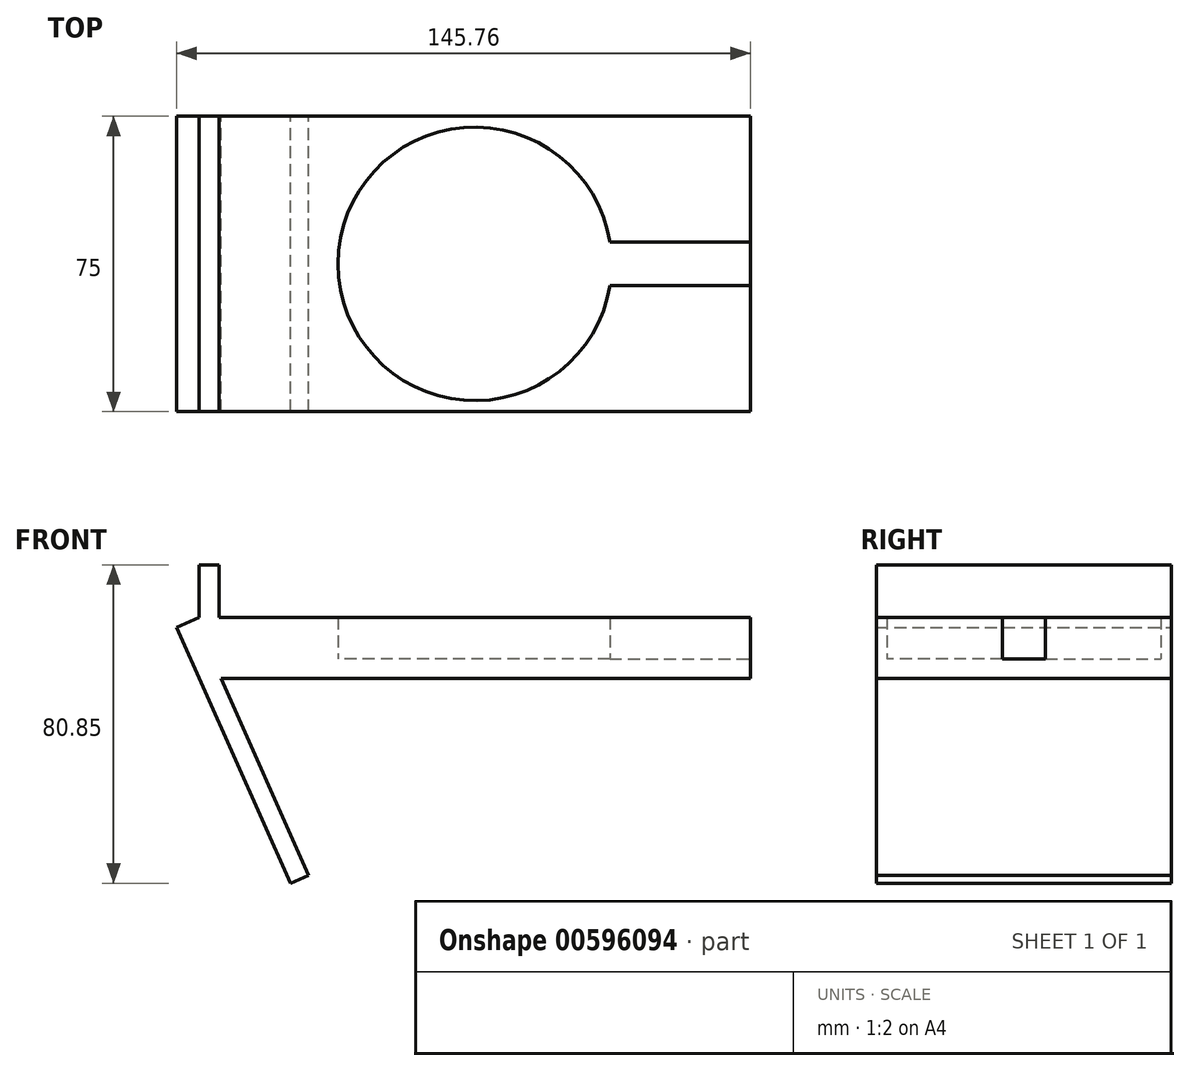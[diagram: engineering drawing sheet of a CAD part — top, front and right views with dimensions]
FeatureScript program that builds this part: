
annotation { "Feature Type Name" : "Feature", "Feature Type Description" : "" }
export const myFeature = defineFeature(function(context is Context, id is Id, definition is map)
    precondition{}
    {
        {
            var Q0;
            Q0=qCreatedBy(makeId("Top.planeOp"),FACE);
            var sketch = newSketch(context, id + "F0", { "sketchPlane" : qUnion([Q0])});
            skLineSegment(sketch, "E0.bottom", {"start": v(70, -37.5) * mm, "end": v(-70, -37.5) * mm});
            skLineSegment(sketch, "E0.top", {"start": v(70, 37.5) * mm, "end": v(-70, 37.5) * mm});
            skLineSegment(sketch, "E0.left", {"start": v(70, -37.5) * mm, "end": v(70, 37.5) * mm});
            skLineSegment(sketch, "E0.right", {"start": v(-70, -37.5) * mm, "end": v(-70, 37.5) * mm});
            skPoint(sketch, "E0.middle", {"position": v(0, 0) * mm});
            skLineSegment(sketch, "E1.bottom", {"start": v(34.31, 5.5) * mm, "end": v(70, 5.5) * mm});
            skLineSegment(sketch, "E1.top", {"start": v(34.31, -5.5) * mm, "end": v(70, -5.5) * mm});
            skLineSegment(sketch, "E1.left", {"start": v(34.31, 5.5) * mm, "end": v(34.31, -5.5) * mm, "construction": true});
            skLineSegment(sketch, "E1.right", {"start": v(70, 5.5) * mm, "end": v(70, -5.5) * mm});
            skPoint(sketch, "E2", {"position": v(34.31, 0) * mm});
            skArc(sketch, "E3", {"start": v(34.31, 5.5) * mm, "mid": v(-34.75, 0) * mm, "end": v(34.31, -5.5) * mm});
            skSolve(sketch);
        }
        {
            var Q0;
            {var subQ4=sQuery(id+"F0.wireOp",EDGE,"E0.bottom");Q0=makeQuery(id+"F0.imprint","IMPRINT",FACE,{"disambiguationData":[TD([[makeQuery(id+"F0.imprint","IMPRINT",EDGE,{"derivedFrom":subQ4}),-1.0]])]});}
            extrude(context, id + "F1", {"entities" : qUnion([Q0]), "depth" : 10.5 * mm, "offsetDistance" : 25 * mm});
        }
        {
            var Q0;
            Q0=qCreatedBy(makeId("Top.planeOp"),FACE);
            var sketch = newSketch(context, id + "F2", { "sketchPlane" : qUnion([Q0])});
            skLineSegment(sketch, "E4.bottom", {"start": v(70, 37.5) * mm, "end": v(-70, 37.5) * mm});
            skLineSegment(sketch, "E4.top", {"start": v(70, -37.5) * mm, "end": v(-70, -37.5) * mm});
            skLineSegment(sketch, "E4.left", {"start": v(70, 37.5) * mm, "end": v(70, -37.5) * mm});
            skLineSegment(sketch, "E4.right", {"start": v(-70, 37.5) * mm, "end": v(-70, -37.5) * mm});
            skPoint(sketch, "E4.middle", {"position": v(0, 0) * mm});
            skSolve(sketch);
        }
        {
            var Q0;
            Q0 = qSketchRegion(id + "F2", true);
            extrude(context, id + "F3", {"entities" : qUnion([Q0]), "operationType" : NewBodyOperationType.ADD, "oppositeDirection" : true, "depth" : 5 * mm, "offsetDistance" : 25 * mm});
        }
        {
            var Q0;
            Q0=qCreatedBy(makeId("Front.planeOp"),FACE);
            var sketch = newSketch(context, id + "F4", { "sketchPlane" : qUnion([Q0])});
            skLineSegment(sketch, "E5.0.0", {"start": v(-70, 10.5) * mm, "end": v(-70, -5) * mm});
            skLineSegment(sketch, "E5.0.1", {"start": v(-70, -5) * mm, "end": v(70, -5) * mm});
            skLineSegment(sketch, "E5.0.2", {"start": v(70, -5) * mm, "end": v(70, 10.5) * mm});
            skLineSegment(sketch, "E5.0.3", {"start": v(70, 10.5) * mm, "end": v(-70, 10.5) * mm});
            skLineSegment(sketch, "E6.bottom", {"start": v(-70, -5) * mm, "end": v(-65.43, -2.97) * mm});
            skLineSegment(sketch, "E6.top", {"start": v(-46.84, -57.02) * mm, "end": v(-42.28, -54.98) * mm});
            skLineSegment(sketch, "E6.left", {"start": v(-70, -5) * mm, "end": v(-46.84, -57.02) * mm});
            skLineSegment(sketch, "E6.right", {"start": v(-65.43, -2.97) * mm, "end": v(-42.28, -54.98) * mm});
            skLineSegment(sketch, "E7", {"start": v(-46.84, -57.02) * mm, "end": v(70, -5) * mm, "construction": true});
            skLineSegment(sketch, "E8", {"start": v(-70, 10.5) * mm, "end": v(-75.76, 7.94) * mm});
            skLineSegment(sketch, "E9", {"start": v(-75.76, 7.94) * mm, "end": v(-70, -5) * mm});
            skSolve(sketch);
        }
        {
            var Q0;
            Q0 = qSketchRegion(id + "F4", true);
            var Q1;
            Q1=makeQuery(id+"F3.boolean.opBoolean","MERGE",FACE,{"derivedFrom":[makeQuery(id+"F1.opExtrude","SWEPT_FACE",FACE,{"disambiguationData":[OSD([sQuery(id+"F0.wireOp",EDGE,"E0.bottom")])]}),makeQuery(id+"F3.opExtrude","SWEPT_FACE",FACE,{"disambiguationData":[OSD([sQuery(id+"F2.wireOp",EDGE,"E4.top")])]})]});
            var Q2;
            Q2=makeQuery(id+"F3.boolean.opBoolean","MERGE",FACE,{"derivedFrom":[makeQuery(id+"F1.opExtrude","SWEPT_FACE",FACE,{"disambiguationData":[OSD([sQuery(id+"F0.wireOp",EDGE,"E0.top")])]}),makeQuery(id+"F3.opExtrude","SWEPT_FACE",FACE,{"disambiguationData":[OSD([sQuery(id+"F2.wireOp",EDGE,"E4.bottom")])]})]});
            extrude(context, id + "F5", {"entities" : qUnion([Q0]), "operationType" : NewBodyOperationType.ADD, "endBound" : BoundingType.UP_TO_SURFACE, "depth" : 25 * mm, "endBoundEntityFace" : qUnion([Q1]), "offsetDistance" : 25 * mm, "hasSecondDirection" : true, "secondDirectionBound" : SecondDirectionBoundingType.UP_TO_SURFACE, "secondDirectionOppositeDirection" : true, "secondDirectionDepth" : 25 * mm, "secondDirectionBoundEntityFace" : qUnion([Q2])});
        }
        {
            var Q0;
            Q0=makeQuery(id+"F0.imprint","IMPRINT",FACE,{"disambiguationData":[TD([[makeQuery(id+"F0.imprint","IMPRINT",EDGE,{"derivedFrom":sQuery(id+"F0.wireOp",EDGE,"E1.bottom")}),-1.0]])]});
            var Q1;
            Q1=sQuery(id+"F0.wireOp",EDGE,"E3");
            var Q2;
            Q2=sQuery(id+"F0.wireOp",EDGE,"E1.bottom");
            var Q3;
            Q3=sQuery(id+"F0.wireOp",EDGE,"E1.right");
            var Q4;
            Q4=sQuery(id+"F0.wireOp",EDGE,"E1.top");
            var Q5;
            Q5=makeQuery(id+"F5.boolean.opBoolean","MERGE",FACE,{"derivedFrom":[makeQuery(id+"F1.opExtrude","CAP_FACE",FACE,{"disambiguationData":[OSD([sQuery(id+"F0.wireOp",EDGE,"E0.bottom"),sQuery(id+"F0.wireOp",EDGE,"E0.top"),sQuery(id+"F0.wireOp",EDGE,"E0.left"),sQuery(id+"F0.wireOp",EDGE,"E0.right"),sQuery(id+"F0.wireOp",EDGE,"E1.bottom"),sQuery(id+"F0.wireOp",EDGE,"E1.top"),sQuery(id+"F0.wireOp",EDGE,"E3")])],"isStart":false}),makeQuery(id+"F5.opExtrude","SWEPT_FACE",FACE,{"disambiguationData":[OSD([sQuery(id+"F4.wireOp",EDGE,"E5.0.3")])]})]});
            extrude(context, id + "F6", {"entities" : qUnion([Q0]), "operationType" : NewBodyOperationType.REMOVE, "surfaceEntities" : qUnion([Q1, Q2, Q3, Q4]), "endBound" : BoundingType.UP_TO_SURFACE, "depth" : 27.1 * mm, "endBoundEntityFace" : qUnion([Q5]), "offsetDistance" : 25 * mm});
        }
        {
            var Q0;
            Q0=makeQuery(id+"F5.boolean.opBoolean","MERGE",FACE,{"derivedFrom":[makeQuery(id+"F1.opExtrude","CAP_FACE",FACE,{"disambiguationData":[OSD([sQuery(id+"F0.wireOp",EDGE,"E0.bottom"),sQuery(id+"F0.wireOp",EDGE,"E0.top"),sQuery(id+"F0.wireOp",EDGE,"E0.left"),sQuery(id+"F0.wireOp",EDGE,"E0.right"),sQuery(id+"F0.wireOp",EDGE,"E1.bottom"),sQuery(id+"F0.wireOp",EDGE,"E1.top"),sQuery(id+"F0.wireOp",EDGE,"E3")])],"isStart":false}),makeQuery(id+"F5.opExtrude","SWEPT_FACE",FACE,{"disambiguationData":[OSD([sQuery(id+"F4.wireOp",EDGE,"E5.0.3")])]})]});
            var sketch = newSketch(context, id + "F7", { "sketchPlane" : qUnion([Q0])});
            skLineSegment(sketch, "E10.bottom", {"start": v(-70, 37.5) * mm, "end": v(-65, 37.5) * mm});
            skLineSegment(sketch, "E10.top", {"start": v(-70, -37.5) * mm, "end": v(-65, -37.5) * mm});
            skLineSegment(sketch, "E10.left", {"start": v(-70, 37.5) * mm, "end": v(-70, -37.5) * mm});
            skLineSegment(sketch, "E10.right", {"start": v(-65, 37.5) * mm, "end": v(-65, -37.5) * mm});
            skSolve(sketch);
        }
        {
            var Q0;
            Q0=makeQuery(id+"F7.imprint","IMPRINT",FACE,{"disambiguationData":[TD([[makeQuery(id+"F7.imprint","IMPRINT",EDGE,{"derivedFrom":sQuery(id+"F7.wireOp",EDGE,"E10.bottom")}),1.0]])]});
            extrude(context, id + "F8", {"entities" : qUnion([Q0]), "operationType" : NewBodyOperationType.ADD, "depth" : 13.33 * mm, "offsetDistance" : 25 * mm});
        }
    });
